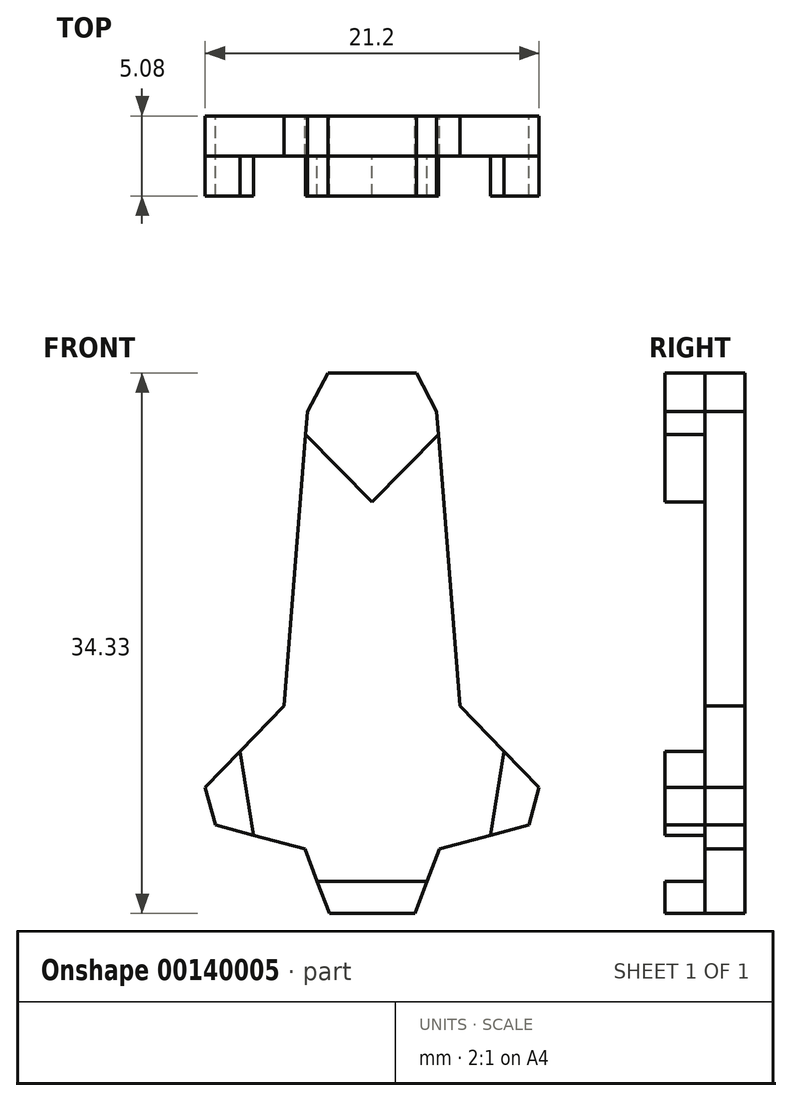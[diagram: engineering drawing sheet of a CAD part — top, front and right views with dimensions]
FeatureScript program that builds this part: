
annotation { "Feature Type Name" : "Feature", "Feature Type Description" : "" }
export const myFeature = defineFeature(function(context is Context, id is Id, definition is map)
    precondition{}
    {
        {
            var Q0;
            Q0=qCreatedBy(makeId("Front.planeOp"),FACE);
            var sketch = newSketch(context, id + "F0", { "sketchPlane" : qUnion([Q0])});
            skLineSegment(sketch, "E0", {"start": v(-2.71, -21.71) * mm, "end": v(-4.28, -17.6) * mm});
            skLineSegment(sketch, "E1", {"start": v(-4.28, -17.6) * mm, "end": v(-9.96, -16.09) * mm});
            skLineSegment(sketch, "E2", {"start": v(-9.96, -16.09) * mm, "end": v(-10.6, -13.7) * mm});
            skLineSegment(sketch, "E3", {"start": v(-4.1, 10.2) * mm, "end": v(-2.82, 12.62) * mm});
            skLineSegment(sketch, "E4.MirrorCS", {"start": v(4.1, 10.2) * mm, "end": v(2.82, 12.62) * mm});
            skLineSegment(sketch, "E5.MirrorCS", {"start": v(4.28, -17.6) * mm, "end": v(9.96, -16.09) * mm});
            skLineSegment(sketch, "E6.MirrorCS", {"start": v(2.71, -21.71) * mm, "end": v(4.28, -17.6) * mm});
            skLineSegment(sketch, "E7.MirrorCS", {"start": v(9.96, -16.09) * mm, "end": v(10.6, -13.7) * mm});
            skLineSegment(sketch, "E8", {"start": v(-2.71, -21.71) * mm, "end": v(2.71, -21.71) * mm});
            skLineSegment(sketch, "E9", {"start": v(-2.82, 12.62) * mm, "end": v(2.82, 12.62) * mm});
            skLineSegment(sketch, "E10", {"start": v(-10.6, -13.7) * mm, "end": v(-5.58, -8.53) * mm});
            skLineSegment(sketch, "E11", {"start": v(-5.58, -8.53) * mm, "end": v(-4.1, 10.2) * mm});
            skLineSegment(sketch, "E12.MirrorCS", {"start": v(5.58, -8.53) * mm, "end": v(4.1, 10.2) * mm});
            skLineSegment(sketch, "E13.MirrorCS", {"start": v(10.6, -13.7) * mm, "end": v(5.58, -8.53) * mm});
            skSolve(sketch);
        }
        {
            var Q0;
            Q0 = qSketchRegion(id + "F0", true);
            extrude(context, id + "F1", {"entities" : qUnion([Q0]), "depth" : 2.54 * mm, "offsetDistance" : 25.4 * mm});
        }
        {
            var Q0;
            Q0=makeQuery(id+"F1.opExtrude","CAP_FACE",FACE,{"disambiguationData":[OSD([sQuery(id+"F0.wireOp",EDGE,"E0"),sQuery(id+"F0.wireOp",EDGE,"E1"),sQuery(id+"F0.wireOp",EDGE,"E2"),sQuery(id+"F0.wireOp",EDGE,"E3"),sQuery(id+"F0.wireOp",EDGE,"E4.MirrorCS"),sQuery(id+"F0.wireOp",EDGE,"E5.MirrorCS"),sQuery(id+"F0.wireOp",EDGE,"E6.MirrorCS"),sQuery(id+"F0.wireOp",EDGE,"E7.MirrorCS"),sQuery(id+"F0.wireOp",EDGE,"E8"),sQuery(id+"F0.wireOp",EDGE,"E9"),sQuery(id+"F0.wireOp",EDGE,"E10"),sQuery(id+"F0.wireOp",EDGE,"E11"),sQuery(id+"F0.wireOp",EDGE,"E12.MirrorCS"),sQuery(id+"F0.wireOp",EDGE,"E13.MirrorCS")])],"isStart":false});
            var sketch = newSketch(context, id + "F2", { "sketchPlane" : qUnion([Q0])});
            skLineSegment(sketch, "E14", {"start": v(2.82, 12.62) * mm, "end": v(-2.82, 12.62) * mm});
            skLineSegment(sketch, "E15", {"start": v(-2.82, 12.62) * mm, "end": v(-4.1, 10.2) * mm});
            skLineSegment(sketch, "E16", {"start": v(-4.1, 10.2) * mm, "end": v(-4.22, 8.71) * mm});
            skLineSegment(sketch, "E17", {"start": v(4.22, 8.71) * mm, "end": v(4.1, 10.2) * mm});
            skLineSegment(sketch, "E18", {"start": v(4.1, 10.2) * mm, "end": v(2.82, 12.62) * mm});
            skLineSegment(sketch, "E19", {"start": v(-4.22, 8.71) * mm, "end": v(0, 4.43) * mm});
            skLineSegment(sketch, "E20", {"start": v(0, 4.43) * mm, "end": v(4.22, 8.71) * mm});
            skSolve(sketch);
        }
        {
            var Q0;
            Q0 = qSketchRegion(id + "F2", true);
            extrude(context, id + "F3", {"entities" : qUnion([Q0]), "depth" : 2.54 * mm, "offsetDistance" : 25.4 * mm});
        }
        {
            var Q0;
            Q0=makeQuery(id+"F1.opExtrude","CAP_FACE",FACE,{"disambiguationData":[OSD([sQuery(id+"F0.wireOp",EDGE,"E0"),sQuery(id+"F0.wireOp",EDGE,"E1"),sQuery(id+"F0.wireOp",EDGE,"E2"),sQuery(id+"F0.wireOp",EDGE,"E3"),sQuery(id+"F0.wireOp",EDGE,"E4.MirrorCS"),sQuery(id+"F0.wireOp",EDGE,"E5.MirrorCS"),sQuery(id+"F0.wireOp",EDGE,"E6.MirrorCS"),sQuery(id+"F0.wireOp",EDGE,"E7.MirrorCS"),sQuery(id+"F0.wireOp",EDGE,"E8"),sQuery(id+"F0.wireOp",EDGE,"E9"),sQuery(id+"F0.wireOp",EDGE,"E10"),sQuery(id+"F0.wireOp",EDGE,"E11"),sQuery(id+"F0.wireOp",EDGE,"E12.MirrorCS"),sQuery(id+"F0.wireOp",EDGE,"E13.MirrorCS")])],"isStart":false});
            var sketch = newSketch(context, id + "F4", { "sketchPlane" : qUnion([Q0])});
            skLineSegment(sketch, "E21", {"start": v(-8.38, -11.42) * mm, "end": v(-10.6, -13.7) * mm});
            skLineSegment(sketch, "E22", {"start": v(-10.6, -13.7) * mm, "end": v(-9.96, -16.09) * mm});
            skLineSegment(sketch, "E23", {"start": v(-9.96, -16.09) * mm, "end": v(-7.53, -16.73) * mm});
            skLineSegment(sketch, "E24", {"start": v(-7.53, -16.73) * mm, "end": v(-8.38, -11.42) * mm});
            skLineSegment(sketch, "E25.MirrorCS", {"start": v(9.96, -16.09) * mm, "end": v(7.53, -16.73) * mm});
            skLineSegment(sketch, "E26.MirrorCS", {"start": v(7.53, -16.73) * mm, "end": v(8.38, -11.42) * mm});
            skLineSegment(sketch, "E27.MirrorCS", {"start": v(8.38, -11.42) * mm, "end": v(10.6, -13.7) * mm});
            skLineSegment(sketch, "E28.MirrorCS", {"start": v(10.6, -13.7) * mm, "end": v(9.96, -16.09) * mm});
            skLineSegment(sketch, "E29", {"start": v(-2.71, -21.71) * mm, "end": v(2.71, -21.71) * mm});
            skLineSegment(sketch, "E30", {"start": v(2.71, -21.71) * mm, "end": v(3.5, -19.66) * mm});
            skLineSegment(sketch, "E31", {"start": v(3.5, -19.66) * mm, "end": v(-3.5, -19.66) * mm});
            skLineSegment(sketch, "E32", {"start": v(-3.5, -19.66) * mm, "end": v(-2.71, -21.71) * mm});
            skSolve(sketch);
        }
        {
            var Q0;
            Q0 = qSketchRegion(id + "F4", true);
            extrude(context, id + "F5", {"entities" : qUnion([Q0]), "depth" : 2.54 * mm, "offsetDistance" : 25.4 * mm});
        }
    });
